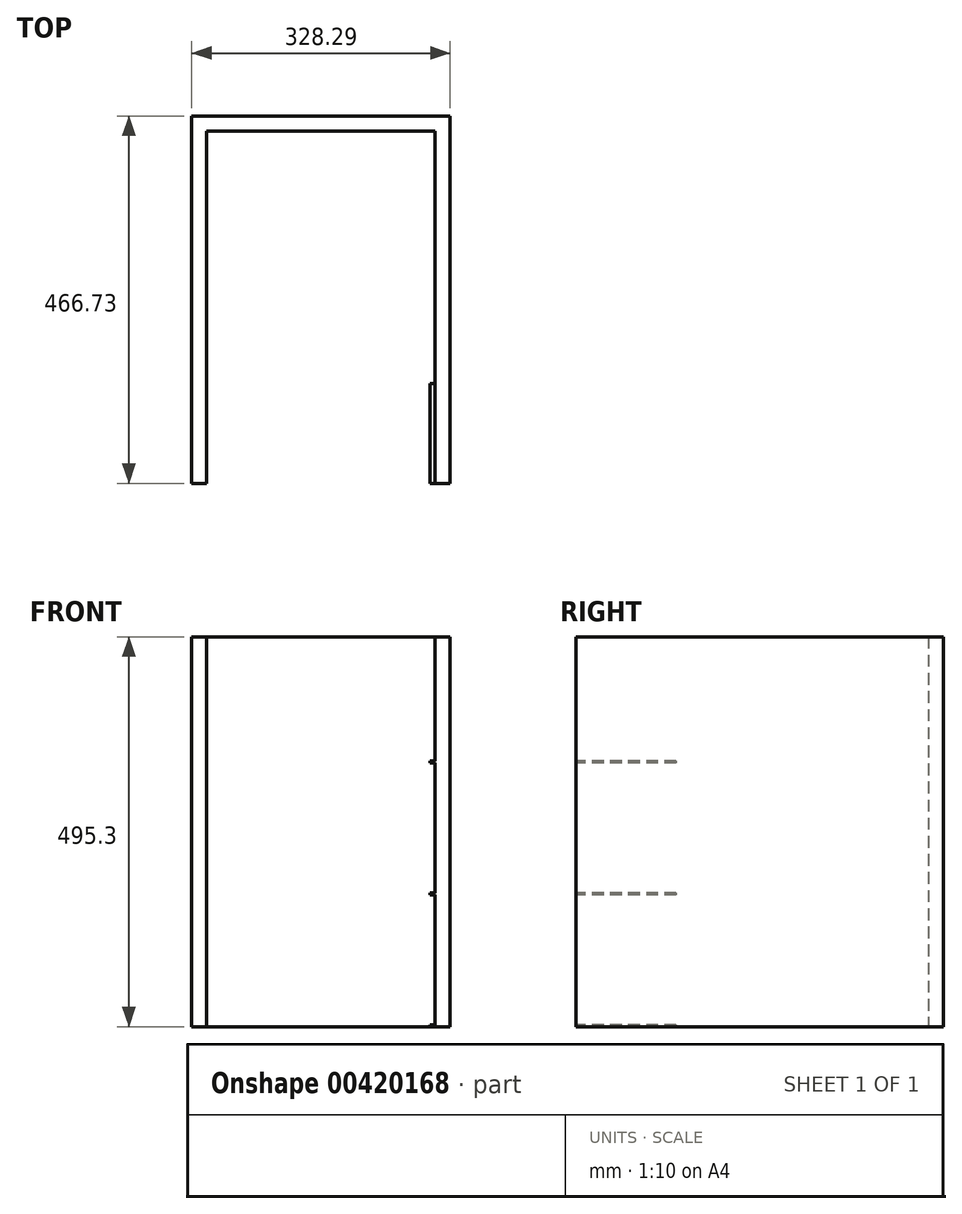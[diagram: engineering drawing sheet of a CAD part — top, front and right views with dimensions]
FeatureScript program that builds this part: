
annotation { "Feature Type Name" : "Feature", "Feature Type Description" : "" }
export const myFeature = defineFeature(function(context is Context, id is Id, definition is map)
    precondition{}
    {
        {
            var Q0;
            Q0=qCreatedBy(makeId("Top.planeOp"),FACE);
            var sketch = newSketch(context, id + "F0", { "sketchPlane" : qUnion([Q0])});
            skLineSegment(sketch, "E0.bottom", {"start": v(0, 0) * mm, "end": v(-244.47, 0) * mm});
            skLineSegment(sketch, "E0.top", {"start": v(0, -422.28) * mm, "end": v(-244.47, -422.28) * mm});
            skLineSegment(sketch, "E0.left", {"start": v(0, 0) * mm, "end": v(0, -422.28) * mm});
            skLineSegment(sketch, "E0.right", {"start": v(-244.47, 0) * mm, "end": v(-244.47, -422.28) * mm});
            skLineSegment(sketch, "E1.0", {"start": v(12.7, -434.98) * mm, "end": v(-257.17, -434.98) * mm});
            skLineSegment(sketch, "E1.1", {"start": v(12.7, 12.7) * mm, "end": v(12.7, -434.98) * mm});
            skLineSegment(sketch, "E1.2", {"start": v(12.7, 12.7) * mm, "end": v(-257.18, 12.7) * mm});
            skLineSegment(sketch, "E1.3", {"start": v(-257.18, 12.7) * mm, "end": v(-257.17, -434.98) * mm});
            skLineSegment(sketch, "E2", {"start": v(-267.33, -434.98) * mm, "end": v(-267.33, 12.7) * mm});
            skLineSegment(sketch, "E3", {"start": v(-267.33, 12.7) * mm, "end": v(22.86, 12.7) * mm});
            skLineSegment(sketch, "E4", {"start": v(22.86, 12.7) * mm, "end": v(22.86, -434.98) * mm});
            skLineSegment(sketch, "E5", {"start": v(22.86, -434.98) * mm, "end": v(41.91, -434.97) * mm});
            skLineSegment(sketch, "E6", {"start": v(41.91, -434.97) * mm, "end": v(41.91, 31.75) * mm});
            skLineSegment(sketch, "E7", {"start": v(41.91, 31.75) * mm, "end": v(-286.38, 31.75) * mm});
            skLineSegment(sketch, "E8", {"start": v(-286.38, 31.75) * mm, "end": v(-286.38, -434.98) * mm});
            skLineSegment(sketch, "E9", {"start": v(-286.38, -434.98) * mm, "end": v(-267.33, -434.98) * mm});
            skSolve(sketch);
        }
        {
            var Q0;
            {var subQ4=sQuery(id+"F0.wireOp",EDGE,"E2");Q0=makeQuery(id+"F0.imprint","IMPRINT",FACE,{"disambiguationData":[TD([[makeQuery(id+"F0.imprint","IMPRINT",EDGE,{"derivedFrom":subQ4}),1.0]])]});}
            extrude(context, id + "F1", {"entities" : qUnion([Q0]), "depth" : 495.3 * mm});
        }
        {
            var Q0;
            Q0=makeQuery(id+"F1.opExtrude","SWEPT_FACE",FACE,{"disambiguationData":[OSD([sQuery(id+"F0.wireOp",EDGE,"E5")])]});
            var sketch = newSketch(context, id + "F2", { "sketchPlane" : qUnion([Q0])});
            skLineSegment(sketch, "E10.bottom", {"start": v(22.86, 0) * mm, "end": v(16.5, 0) * mm});
            skLineSegment(sketch, "E10.top", {"start": v(22.86, 2.54) * mm, "end": v(16.5, 2.54) * mm});
            skLineSegment(sketch, "E10.left", {"start": v(22.86, 0) * mm, "end": v(22.86, 2.54) * mm});
            skLineSegment(sketch, "E10.right", {"start": v(16.5, 0) * mm, "end": v(16.5, 2.54) * mm});
            skLineSegment(sketch, "E11.bottom", {"start": v(22.86, 170.18) * mm, "end": v(16.5, 170.18) * mm});
            skLineSegment(sketch, "E11.top", {"start": v(22.86, 167.64) * mm, "end": v(16.5, 167.64) * mm});
            skLineSegment(sketch, "E11.left", {"start": v(22.86, 170.18) * mm, "end": v(22.86, 167.64) * mm});
            skLineSegment(sketch, "E11.right", {"start": v(16.5, 170.18) * mm, "end": v(16.5, 167.64) * mm});
            skLineSegment(sketch, "E12.bottom", {"start": v(22.86, 337.82) * mm, "end": v(16.5, 337.82) * mm});
            skLineSegment(sketch, "E12.top", {"start": v(22.86, 335.28) * mm, "end": v(16.5, 335.28) * mm});
            skLineSegment(sketch, "E12.left", {"start": v(22.86, 337.82) * mm, "end": v(22.86, 335.28) * mm});
            skLineSegment(sketch, "E12.right", {"start": v(16.5, 337.82) * mm, "end": v(16.5, 335.28) * mm});
            skSolve(sketch);
        }
        {
            var Q0;
            Q0 = qSketchRegion(id + "F2", true);
            extrude(context, id + "F3", {"entities" : qUnion([Q0]), "operationType" : NewBodyOperationType.ADD, "oppositeDirection" : true, "depth" : 127 * mm});
        }
    });
